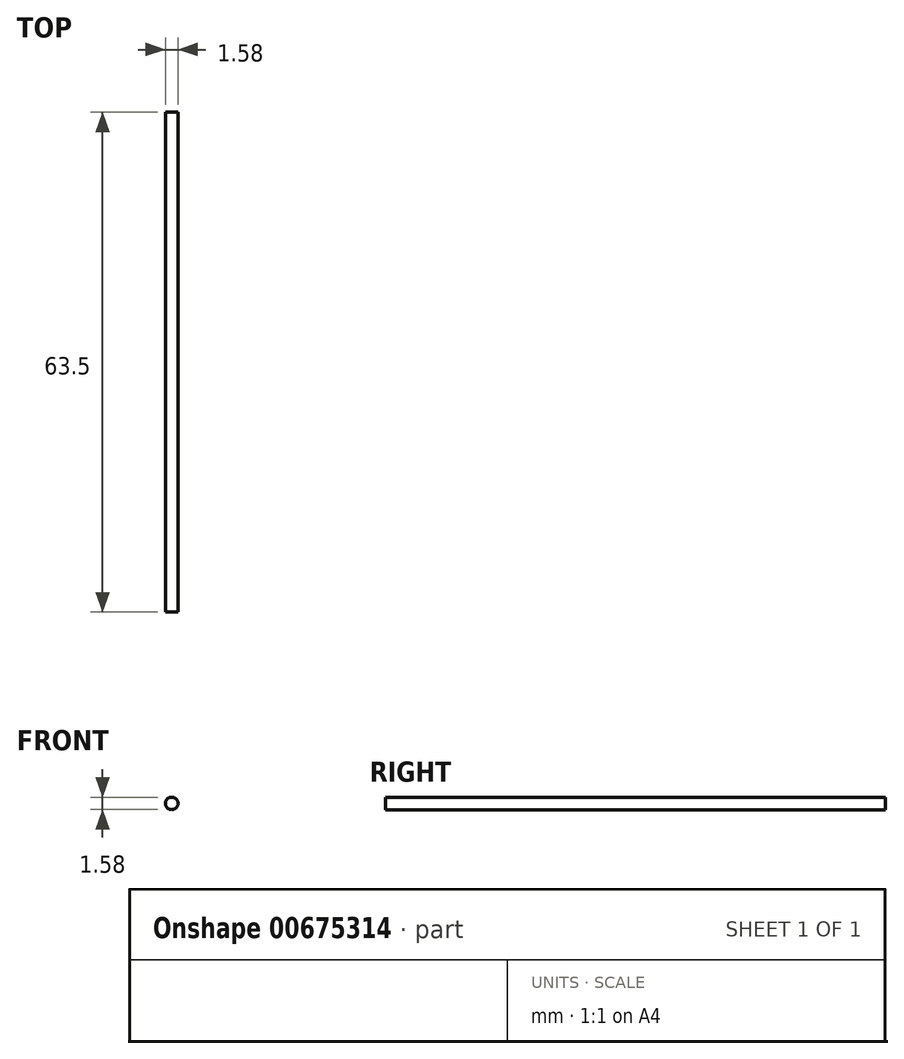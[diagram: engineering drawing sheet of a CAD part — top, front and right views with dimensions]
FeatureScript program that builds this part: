
annotation { "Feature Type Name" : "Feature", "Feature Type Description" : "" }
export const myFeature = defineFeature(function(context is Context, id is Id, definition is map)
    precondition{}
    {
        {
            var Q0;
            Q0=qCreatedBy(makeId("Front.planeOp"),FACE);
            var sketch = newSketch(context, id + "F0", { "sketchPlane" : qUnion([Q0])});
            skCircle(sketch, "E0", {"center": v(0, 0) * mm, "radius": 0.8 * mm});
            skSolve(sketch);
        }
        {
            var Q0;
            Q0=makeQuery(id+"F0.imprint","IMPRINT",FACE,{"disambiguationData":[TD([[makeQuery(id+"F0.imprint","IMPRINT",EDGE,{"derivedFrom":sQuery(id+"F0.wireOp",EDGE,"E0")}),1.0]])]});
            extrude(context, id + "F1", {"entities" : qUnion([Q0]), "oppositeDirection" : true, "depth" : 63.5 * mm, "offsetDistance" : 25.4 * mm});
        }
    });
